# Revit family: Wall_Hung_Lavatory_Sink-Elkay- ELVWO2219_1_3_CS3
name_source: partatom
category: Plumbing Fixtures
units: mm (PartAtom-declared; Revit-internal decimal feet)

## family parameters
Cut with Voids When Loaded = No
Host = Face
Maintain Annotation Orientation = No
OmniClass Number = 23.45.05.14.14
OmniClass Title = Sinks/Lavatories
Part Type = Normal
Room Calculation Point = No
Round Connector Dimension = Use Diameter
Shared = No

## types (4) — shared parameters
Approx. Shipping Weight (lbs) = 16
Assembly Code = D2010300
Back Splash Height = 2.5 "
Bowl 1 Dimensions = 16 inch x 11 1/2 inch x 5 1/2 inch
Bowl Depth = 5.5 "
Bowl Length = 16 "
Bowl Width = 11.5 "
Default Elevation = 48 "
Depth of Sink = 10 "
Description = Stainless Steel 22 inch x 19 inch x 5 1/2 inch Wall Hung Lavatory Sink with Overflow
Drain Location = Rear Center
Drain Size = 1.5 "
Gauge = 18
Installation Type = Wall Hung
Length of Sink = 22 "
Main Material = Finish-Elkay-Stainless Steel
Manufacturer = Elkay Manufacturer Company
Manufacturer Brand = Elkay (by Zurn Elkay Water Solutions)
No of Bowls = 1
Outlet Connection Size (inch) = 1.5 "
Product Documentation Link = https://www.elkayfiles.com
Product Installation Sheet URL = https://www.elkayfiles.com
Product Page URL = https://www.elkay.com
Product data URL = https://bimobject.com
R for masking = 1.75 "
Repair Parts URL = https://www.elkayfiles.com
Sink Dimensions = 22 inch x 19 inch x 10 inch
URL = https://www.elkay.com
Width of Sink = 19 "
zero-valued in all types: CWFU, HWFU, WFU

## per-type parameters (varying)
| type | C/C distance between the 2 Holes | Center Hole | Left and Right Holes | Model | Product Weight (lbs) |
| ELVWO2219 (Wall Hung Lavatory Sink with Overflow) | 4 " | No | No | ELVWO2219 | 15 |
| ELVWO22191 (Wall Hung Lavatory Sink with Overflow) | 4 " | Yes | No | ELVWO22191 | 15 |
| ELVWO22193 (Wall Hung Lavatory Sink with Overflow) | 8 " | Yes | Yes | ELVWO22193 | 15 |
| ELVWO2219CS3 (Wall Hung Lavatory Sink with Overflow) | 4 " | Yes | Yes | ELVWO2219CS3 | 11 |

## geometry (parser evidence)
native form markers: Sweep x5
no freeform markers — native parametric forms only
